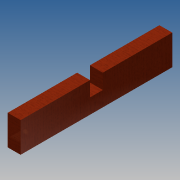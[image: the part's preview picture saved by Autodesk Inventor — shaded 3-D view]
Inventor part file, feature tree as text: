
AUTODESK INVENTOR PART (.ipt)
format: ipt  version: 2014 SP1 (Build 180222100, 222)  size: 100,864 bytes
history: native  units: in
note: dims shown in document units (in); Inventor stores cm internally (conversion verified against a paired STEP export)
features: sketch x3, extrude x2, hole x1
ambient origin geometry x8: Origin, YZ Plane, XZ Plane, XY Plane, X Axis, Y Axis, Z Axis, Center Point
bodies: Solid1 (feature_tree)
feature tree (6):
  extrude  "Extrusion1"  Depth=17.7in
  extrude  "Extrusion2"  Depth=1.75in
  hole  "Hole1"  [1 undecoded]
  sketch  "Sketch1"  dims[d0=3.5in d1=17.7in]
  sketch  "Sketch2"  dims[d2=1.5in d3=0.0in d4=1.75in]
  sketch  "Sketch3"  dims[d5=8.1in d6=2.0in d7=0.0in d8=0.25in d9=0.75in d10=0.375in d11=0.25in d12=0.5635in d13=0.5in d14=0.8108in]
note: 1 required parameter value undecoded (feature->parameter linkage not recoverable at this tier; creation-order binding heuristic only, values carry confidence <= 0.55)
